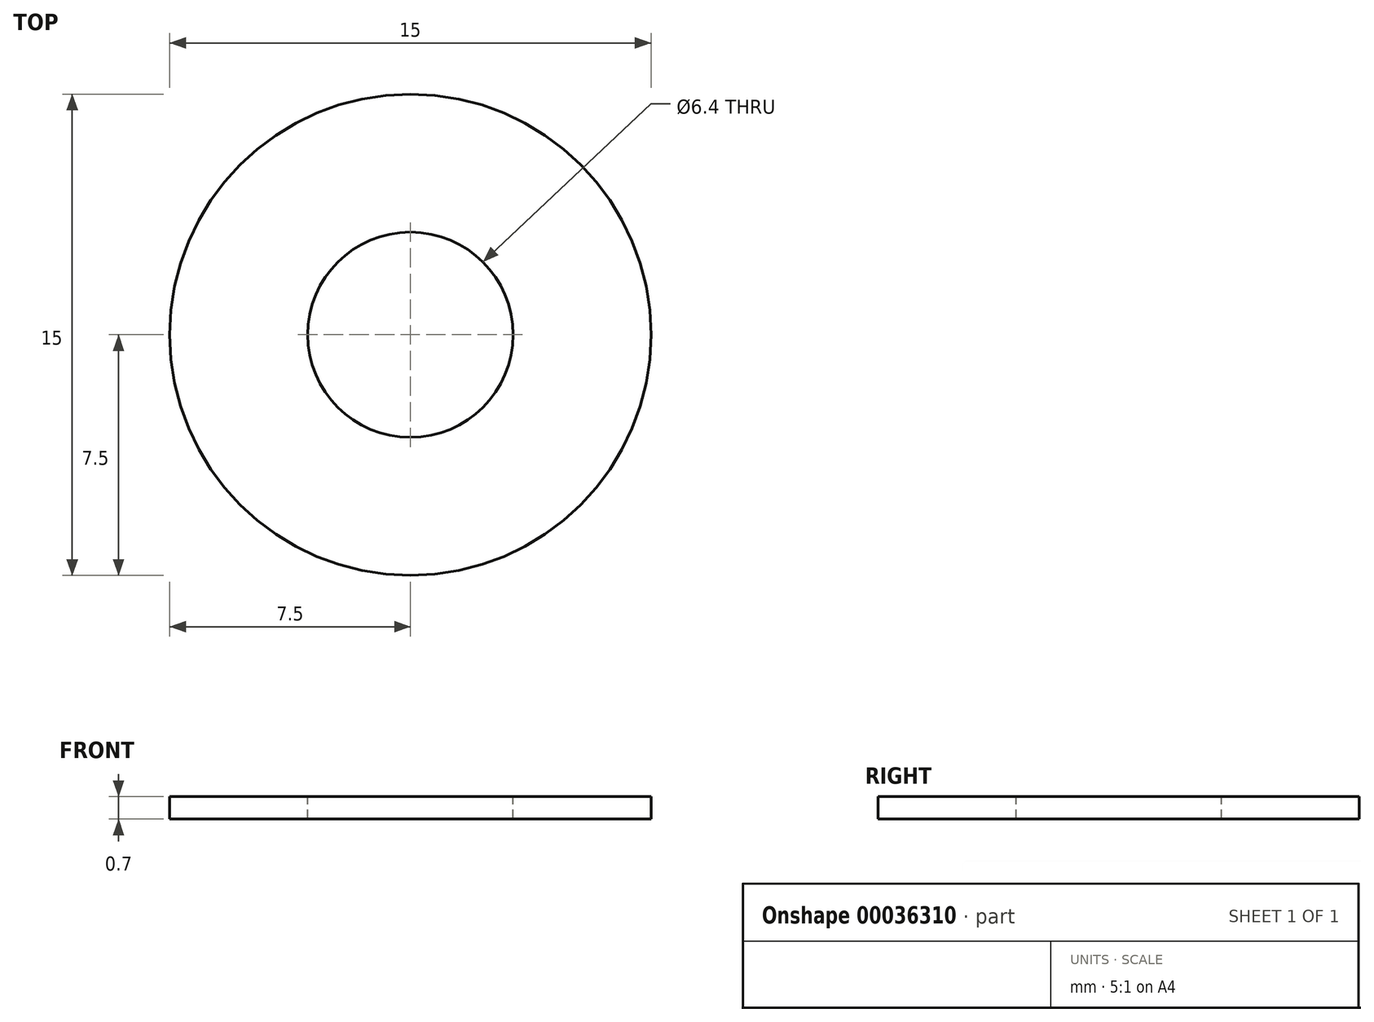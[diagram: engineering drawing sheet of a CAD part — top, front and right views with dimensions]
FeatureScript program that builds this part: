
annotation { "Feature Type Name" : "Feature", "Feature Type Description" : "" }
export const myFeature = defineFeature(function(context is Context, id is Id, definition is map)
    precondition{}
    {
        {
            var Q0;
            Q0=qCreatedBy(makeId("Top.planeOp"),FACE);
            var sketch = newSketch(context, id + "F0", { "sketchPlane" : qUnion([Q0])});
            skCircle(sketch, "E0", {"center": v(0, 0) * mm, "radius": 7.5 * mm});
            skSolve(sketch);
        }
        {
            var Q0;
            Q0=qSketchRegion(id+"F0",true);
            extrude(context, id + "F1", {"entities" : qUnion([Q0]), "depth" : 0.7 * mm});
        }
        {
            var Q0;
            Q0=makeQuery(id+"F1.opExtrude","CAP_FACE",FACE,{"disambiguationData":[OSD([sQuery(id+"F0.wireOp",EDGE,"E0")])],"isStart":false});
            var sketch = newSketch(context, id + "F2", { "sketchPlane" : qUnion([Q0])});
            skCircle(sketch, "E1", {"center": v(0, 0) * mm, "radius": 3.2 * mm});
            skSolve(sketch);
        }
        {
            var Q0;
            Q0=makeQuery(id+"F2.imprint","IMPRINT",FACE,{"disambiguationData":[TD([[makeQuery(id+"F2.imprint","IMPRINT",EDGE,{"derivedFrom":sQuery(id+"F2.wireOp",EDGE,"E1")}),1.0]])]});
            extrude(context, id + "F3", {"entities" : qUnion([Q0]), "operationType" : NewBodyOperationType.REMOVE, "endBound" : BoundingType.UP_TO_NEXT, "oppositeDirection" : true, "depth" : 25 * mm});
        }
    });
